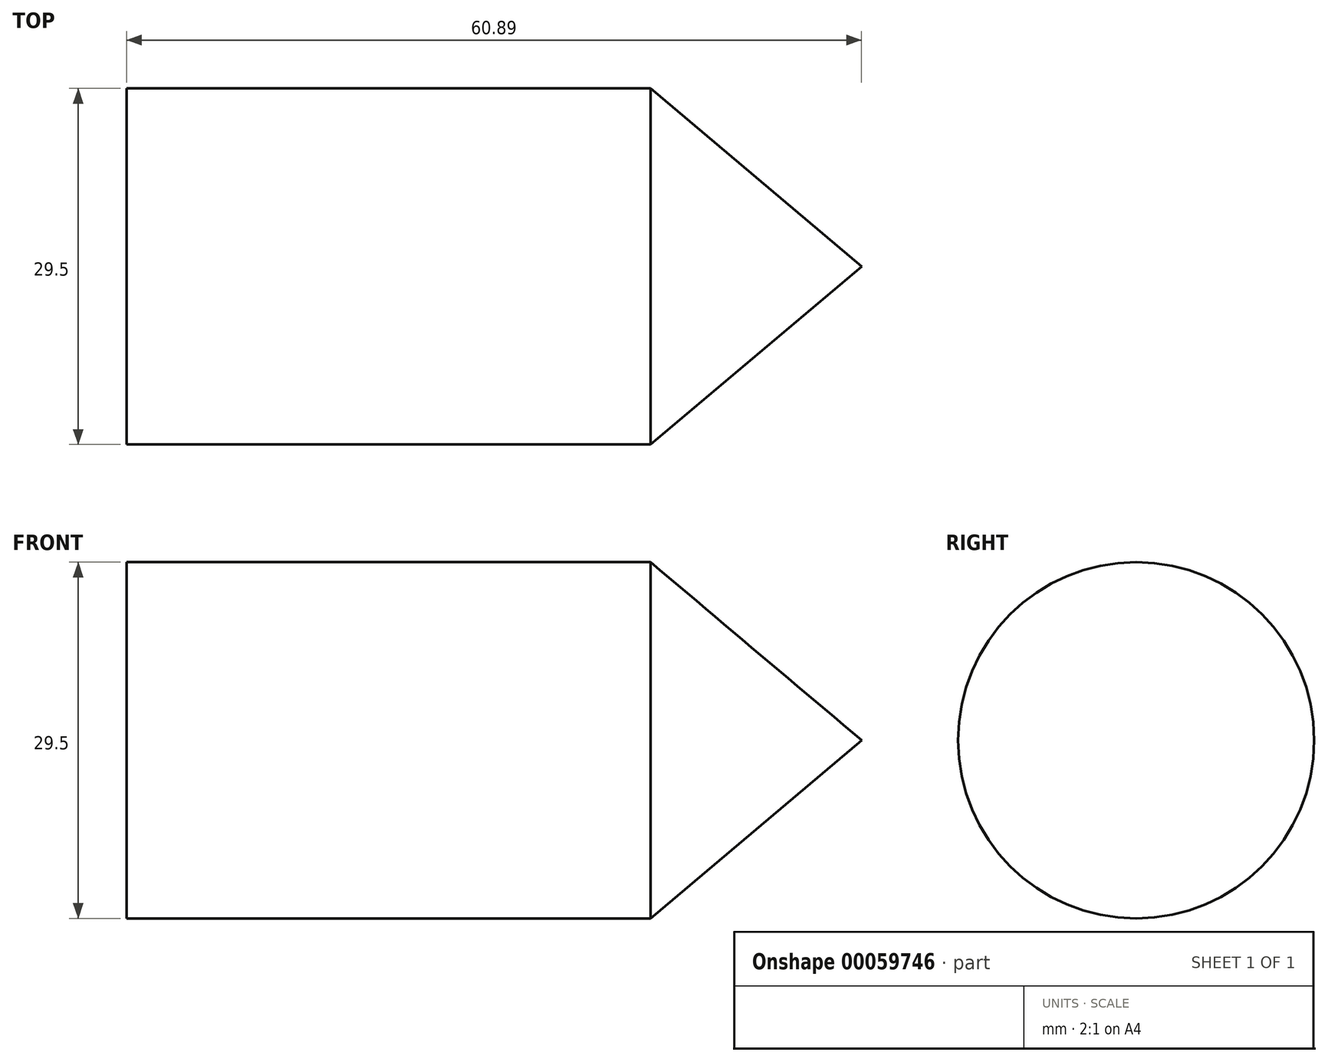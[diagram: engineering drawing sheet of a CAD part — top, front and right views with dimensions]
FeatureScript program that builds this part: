
annotation { "Feature Type Name" : "Feature", "Feature Type Description" : "" }
export const myFeature = defineFeature(function(context is Context, id is Id, definition is map)
    precondition{}
    {
        {
            var Q0;
            Q0=qCreatedBy(makeId("Front.planeOp"),FACE);
            var sketch = newSketch(context, id + "F0", { "sketchPlane" : qUnion([Q0])});
            skLineSegment(sketch, "E0", {"start": v(0, 0) * mm, "end": v(0, 14.75) * mm});
            skLineSegment(sketch, "E1", {"start": v(0, 14.75) * mm, "end": v(43.41, 14.75) * mm});
            skLineSegment(sketch, "E2", {"start": v(43.41, 14.75) * mm, "end": v(60.9, 0) * mm});
            skLineSegment(sketch, "E3", {"start": v(60.9, 0) * mm, "end": v(0, 0) * mm});
            skSolve(sketch);
        }
        {
            var Q0;
            Q0=makeQuery(id+"F0.imprint","IMPRINT",FACE,{"disambiguationData":[TD([[makeQuery(id+"F0.imprint","IMPRINT",EDGE,{"derivedFrom":sQuery(id+"F0.wireOp",EDGE,"E0")}),-1.0]])]});
            var Q1;
            Q1=sQuery(id+"F0.wireOp",EDGE,"E3");
            revolve(context, id + "F1", {"entities" : qUnion([Q0]), "axis" : qUnion([Q1]), "revolveType" : RevolveType.FULL});
        }
    });
